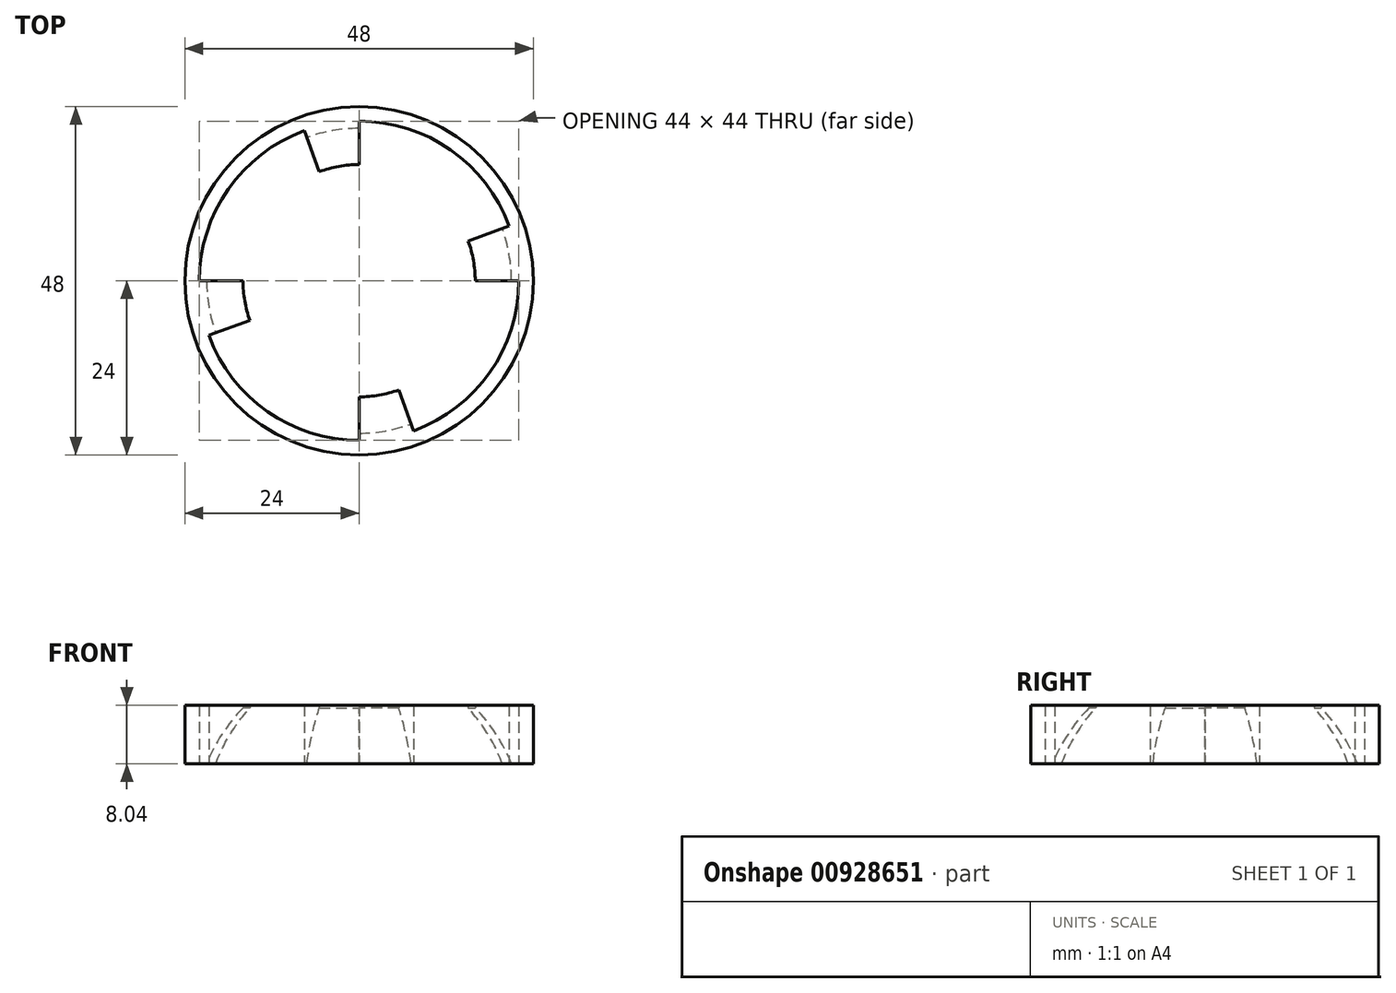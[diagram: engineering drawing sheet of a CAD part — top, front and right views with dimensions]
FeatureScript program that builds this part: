
annotation { "Feature Type Name" : "Feature", "Feature Type Description" : "" }
export const myFeature = defineFeature(function(context is Context, id is Id, definition is map)
    precondition{}
    {
        {
            var Q0;
            Q0=qCreatedBy(makeId("Front.planeOp"),FACE);
            var sketch = newSketch(context, id + "F0", { "sketchPlane" : qUnion([Q0])});
            skLineSegment(sketch, "E0", {"start": v(0, 0) * mm, "end": v(0, 52.54) * mm, "construction": true});
            skLineSegment(sketch, "E1.bottom", {"start": v(16, 0) * mm, "end": v(22, 0) * mm});
            skLineSegment(sketch, "E1.top", {"start": v(16, -8.04) * mm, "end": v(21, -8.04) * mm, "construction": true});
            skLineSegment(sketch, "E1.left", {"start": v(16, 0) * mm, "end": v(16, -0.37) * mm});
            skLineSegment(sketch, "E1.right", {"start": v(22, 0) * mm, "end": v(22, -8.04) * mm});
            skArc(sketch, "E2", {"start": v(16, -0.37) * mm, "mid": v(-20.5, -29.6) * mm, "end": v(21, -8.04) * mm, "construction": true});
            skArc(sketch, "E3", {"start": v(21, -8.04) * mm, "mid": v(18.88, -3.96) * mm, "end": v(16, -0.37) * mm});
            skLineSegment(sketch, "E4", {"start": v(21, -8.04) * mm, "end": v(22, -8.04) * mm});
            skLineSegment(sketch, "E5", {"start": v(16, -0.37) * mm, "end": v(16, -8.04) * mm, "construction": true});
            skPoint(sketch, "E6", {"position": v(19, 0) * mm});
            skSolve(sketch);
        }
        {
            var Q0;
            Q0=qSketchRegion(id+"F0",true);
            var Q1;
            Q1=sQuery(id+"F0.wireOp",EDGE,"E0");
            revolve(context, id + "F1", {"surfaceOperationType" : NewSurfaceOperationType.NEW, "entities" : qUnion([Q0]), "axis" : qUnion([Q1]), "revolveType" : RevolveType.TWO_DIRECTIONS, "angle" : 20 * degree, "angleBack" : 0 * degree});
        }
        {
            var Q0;
            Q0=makeQuery(id+"F1.opRevolve","SWEPT_BODY",BODY,{"disambiguationData":[OSD([sQuery(id+"F0.wireOp",EDGE,"E1.bottom"),sQuery(id+"F0.wireOp",EDGE,"E1.left"),sQuery(id+"F0.wireOp",EDGE,"E1.right"),sQuery(id+"F0.wireOp",EDGE,"E3"),sQuery(id+"F0.wireOp",EDGE,"E4")])]});
            var Q1;
            Q1=sQuery(id+"F0.wireOp",EDGE,"E0");
            circularPattern(context, id + "F2", {"entities" : qUnion([Q0]), "axis" : qUnion([Q1]), "angle" : 360 * degree, "instanceCount" : 4, "equalSpace" : true});
        }
        {
            var Q0;
            Q0=makeQuery(id+"F1.opRevolve","CAP_FACE",FACE,{"disambiguationData":[OSD([sQuery(id+"F0.wireOp",EDGE,"E1.bottom"),sQuery(id+"F0.wireOp",EDGE,"E1.left"),sQuery(id+"F0.wireOp",EDGE,"E1.right"),sQuery(id+"F0.wireOp",EDGE,"E3"),sQuery(id+"F0.wireOp",EDGE,"E4")])],"isStart":false});
            var sketch = newSketch(context, id + "F3", { "sketchPlane" : qUnion([Q0])});
            skSolve(sketch);
        }
        {
            var Q0;
            Q0=makeQuery(id+"F3.imprint","IMPRINT",FACE,{"disambiguationData":[TD([[makeQuery(id+"F3.imprint","IMPRINT",EDGE,{"derivedFrom":makeQuery(id+"F1.opRevolve","CAP_EDGE",EDGE,{"disambiguationData":[OSD([sQuery(id+"F0.wireOp",EDGE,"E1.bottom")])],"isStart":false})}),1.0]])]});
            var sketch = newSketch(context, id + "F4", { "sketchPlane" : qUnion([Q0])});
            skArc(sketch, "E7.0", {"start": v(-21, -8.04) * mm, "mid": v(-18.74, -3.74) * mm, "end": v(-15.63, 0) * mm, "construction": true});
            skArc(sketch, "E8", {"start": v(-15.63, 0) * mm, "mid": v(17.44, -33.38) * mm, "end": v(-16, -0.37) * mm, "construction": true});
            skLineSegment(sketch, "E9.0", {"start": v(-22, 0) * mm, "end": v(-22, -8.04) * mm, "construction": true});
            skLineSegment(sketch, "E10", {"start": v(-15.63, 0) * mm, "end": v(-22, 0) * mm, "construction": true});
            skLineSegment(sketch, "E11", {"start": v(-22, -8.04) * mm, "end": v(-22, 0) * mm, "construction": true});
            skLineSegment(sketch, "E12", {"start": v(-22, -8.04) * mm, "end": v(-24, -8.04) * mm});
            skLineSegment(sketch, "E13", {"start": v(-24, -8.04) * mm, "end": v(-24, 0) * mm});
            skLineSegment(sketch, "E14", {"start": v(-24, 0) * mm, "end": v(-22, 0) * mm});
            skLineSegment(sketch, "E15", {"start": v(-22, -8.04) * mm, "end": v(-22, 0) * mm});
            skSolve(sketch);
        }
        {
            var Q0;
            Q0 = qSketchRegion(id + "F4", true);
            var Q1;
            Q1=sQuery(id+"F0.wireOp",EDGE,"E0");
            revolve(context, id + "F5", {"surfaceOperationType" : NewSurfaceOperationType.NEW, "entities" : qUnion([Q0]), "axis" : qUnion([Q1]), "revolveType" : RevolveType.FULL});
        }
        {
            var Q0;
            Q0=makeQuery(id+"F1.opRevolve","SWEPT_BODY",BODY,{"disambiguationData":[OSD([sQuery(id+"F0.wireOp",EDGE,"E1.bottom"),sQuery(id+"F0.wireOp",EDGE,"E1.left"),sQuery(id+"F0.wireOp",EDGE,"E1.right"),sQuery(id+"F0.wireOp",EDGE,"E3"),sQuery(id+"F0.wireOp",EDGE,"E4")])]});
            var Q1;
            Q1=makeQuery(id+"F2.opPattern","COPY",BODY,{"derivedFrom":makeQuery(id+"F1.opRevolve","SWEPT_BODY",BODY,{"disambiguationData":[OSD([sQuery(id+"F0.wireOp",EDGE,"E1.bottom"),sQuery(id+"F0.wireOp",EDGE,"E1.left"),sQuery(id+"F0.wireOp",EDGE,"E1.right"),sQuery(id+"F0.wireOp",EDGE,"E3"),sQuery(id+"F0.wireOp",EDGE,"E4")])]}),"instanceName":"1"});
            var Q2;
            Q2=makeQuery(id+"F2.opPattern","COPY",BODY,{"derivedFrom":makeQuery(id+"F1.opRevolve","SWEPT_BODY",BODY,{"disambiguationData":[OSD([sQuery(id+"F0.wireOp",EDGE,"E1.bottom"),sQuery(id+"F0.wireOp",EDGE,"E1.left"),sQuery(id+"F0.wireOp",EDGE,"E1.right"),sQuery(id+"F0.wireOp",EDGE,"E3"),sQuery(id+"F0.wireOp",EDGE,"E4")])]}),"instanceName":"2"});
            var Q3;
            Q3=makeQuery(id+"F2.opPattern","COPY",BODY,{"derivedFrom":makeQuery(id+"F1.opRevolve","SWEPT_BODY",BODY,{"disambiguationData":[OSD([sQuery(id+"F0.wireOp",EDGE,"E1.bottom"),sQuery(id+"F0.wireOp",EDGE,"E1.left"),sQuery(id+"F0.wireOp",EDGE,"E1.right"),sQuery(id+"F0.wireOp",EDGE,"E3"),sQuery(id+"F0.wireOp",EDGE,"E4")])]}),"instanceName":"3"});
            var Q4;
            Q4=makeQuery(id+"F5.opRevolve","SWEPT_BODY",BODY,{"disambiguationData":[OSD([sQuery(id+"F4.wireOp",EDGE,"E12"),sQuery(id+"F4.wireOp",EDGE,"E13"),sQuery(id+"F4.wireOp",EDGE,"E14"),sQuery(id+"F4.wireOp",EDGE,"E15")])]});
            booleanBodies(context, id + "F6", {"operationType" : BooleanOperationType.UNION, "tools" : qUnion([Q0, Q1, Q2, Q3, Q4])});
        }
        {
            var Q0;
            Q0=makeQuery(id+"F1.opRevolve","SWEPT_FACE",FACE,{"disambiguationData":[OSD([sQuery(id+"F0.wireOp",EDGE,"E1.bottom")])]});
            var sketch = newSketch(context, id + "F7", { "sketchPlane" : qUnion([Q0])});
            skLineSegment(sketch, "E16.0", {"start": v(16, 0) * mm, "end": v(22, 0) * mm});
            skLineSegment(sketch, "E16.1", {"start": v(15.04, 5.47) * mm, "end": v(20.67, 7.52) * mm});
            skArc(sketch, "E16.3", {"start": v(15.04, 5.47) * mm, "mid": v(15.76, 2.78) * mm, "end": v(16, 0) * mm});
            skPoint(sketch, "E17.orphan", {"position": v(22, 0) * mm});
            skPoint(sketch, "E18.orphan", {"position": v(20.67, 7.52) * mm});
            skArc(sketch, "E19", {"start": v(24, 0) * mm, "mid": v(23.64, 4.17) * mm, "end": v(22.55, 8.2) * mm});
            skArc(sketch, "E20", {"start": v(22.55, 8.2) * mm, "mid": v(-23.64, -4.17) * mm, "end": v(24, 0) * mm, "construction": true});
            skLineSegment(sketch, "E21", {"start": v(20.67, 7.52) * mm, "end": v(22, 0) * mm});
            skSolve(sketch);
        }
        {
            var Q0;
            Q0=makeQuery(id+"F7.imprint","IMPRINT",FACE,{"disambiguationData":[TD([[makeQuery(id+"F7.imprint","IMPRINT",EDGE,{"derivedFrom":sQuery(id+"F7.wireOp",EDGE,"E16.0")}),1.0]])]});
            cPlane(context, id + "F8", {"entities" : qUnion([Q0]), "cplaneType" : CPlaneType.OFFSET, "offset" : 20 * mm, "width" : 150 * mm, "height" : 150 * mm});
        }
        {
            var Q0;
            Q0=qCreatedBy(id+"F8.planeOp",FACE);
            var sketch = newSketch(context, id + "F9", { "sketchPlane" : qUnion([Q0])});
            skPoint(sketch, "E22.0", {"position": v(15.76, 2.78) * mm});
            skLineSegment(sketch, "E23", {"start": v(0, 0) * mm, "end": v(20.19, 3.56) * mm, "construction": true});
            skCircle(sketch, "E24", {"center": v(20.19, 3.56) * mm, "radius": 1 * mm});
            skPoint(sketch, "E25", {"position": v(19.37, 4.13) * mm});
            skPoint(sketch, "E26", {"position": v(21, 2.99) * mm});
            skLineSegment(sketch, "E27", {"start": v(19.37, 4.13) * mm, "end": v(21, 2.99) * mm, "construction": true});
            skLineSegment(sketch, "E28", {"start": v(20.76, 4.38) * mm, "end": v(19.61, 2.74) * mm, "construction": true});
            skLineSegment(sketch, "E29", {"start": v(19.61, 2.74) * mm, "end": v(19.37, 4.13) * mm, "construction": true});
            skPoint(sketch, "E30", {"position": v(19.5, 3.44) * mm});
            skSolve(sketch);
        }
        {
            var Q1;
            Q1=makeQuery(id+"F7.imprint","IMPRINT",FACE,{"disambiguationData":[TD([[makeQuery(id+"F7.imprint","IMPRINT",EDGE,{"derivedFrom":sQuery(id+"F7.wireOp",EDGE,"E16.0")}),1.0]])]});
            var Q2;
            Q2=makeQuery(id+"F9.imprint","IMPRINT",FACE,{"disambiguationData":[TD([[makeQuery(id+"F9.imprint","IMPRINT",EDGE,{"derivedFrom":sQuery(id+"F9.wireOp",EDGE,"E24")}),1.0]])]});
            loft(context, id + "F10", {"sheetProfilesArray" : [{ "sheetProfileEntities" : qUnion([Q1]) }, { "sheetProfileEntities" : qUnion([Q2]) }]});
        }
        {
            var Q0;
            Q0=makeQuery(id+"F10.opLoft","SWEPT_BODY",BODY,{"disambiguationData":[OSD([makeQuery(id+"F7.imprint","IMPRINT",FACE,{"disambiguationData":[TD([[makeQuery(id+"F7.imprint","IMPRINT",EDGE,{"derivedFrom":sQuery(id+"F7.wireOp",EDGE,"E16.0")}),1.0]])]}),makeQuery(id+"F9.imprint","IMPRINT",FACE,{"disambiguationData":[TD([[makeQuery(id+"F9.imprint","IMPRINT",EDGE,{"derivedFrom":sQuery(id+"F9.wireOp",EDGE,"E24")}),1.0]])]})])]});
            var Q1;
            Q1=sQuery(id+"F0.wireOp",EDGE,"E0");
            circularPattern(context, id + "F11", {"entities" : qUnion([Q0]), "axis" : qUnion([Q1]), "angle" : 360 * degree, "instanceCount" : 4, "equalSpace" : true});
        }
        {
            var Q0;
            {var subQ0=makeQuery(id+"F1.opRevolve","SWEPT_FACE",FACE,{"disambiguationData":[OSD([sQuery(id+"F0.wireOp",EDGE,"E1.bottom")])]});Q0=makeQuery(id+"F6.opBoolean","MERGE",FACE,{"derivedFrom":[subQ0,makeQuery(id+"F2.opPattern","COPY",FACE,{"derivedFrom":subQ0,"instanceName":"1"}),makeQuery(id+"F2.opPattern","COPY",FACE,{"derivedFrom":subQ0,"instanceName":"2"}),makeQuery(id+"F5.opRevolve","SWEPT_FACE",FACE,{"disambiguationData":[OSD([sQuery(id+"F4.wireOp",EDGE,"E14")])]})]});}
            extrude(context, id + "F12", {"entities" : qUnion([Q0]), "operationType" : NewBodyOperationType.REMOVE, "depth" : 25 * mm, "offsetDistance" : 25 * mm});
        }
    });
